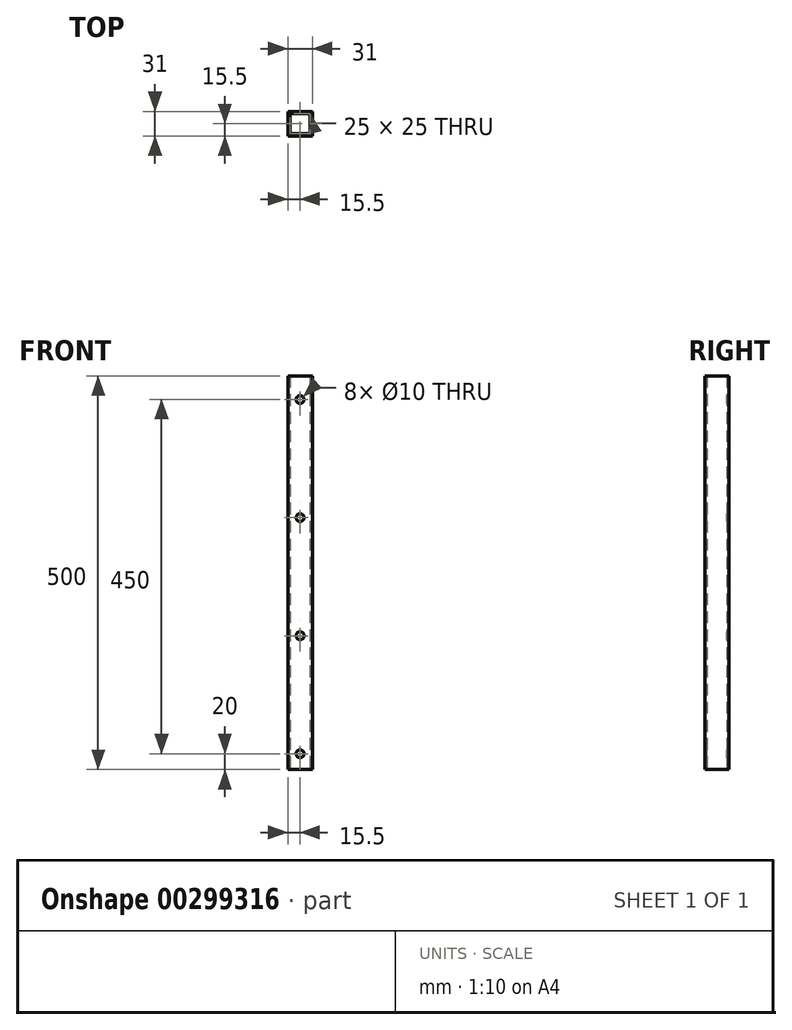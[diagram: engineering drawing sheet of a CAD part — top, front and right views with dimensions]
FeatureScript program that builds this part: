
annotation { "Feature Type Name" : "Feature", "Feature Type Description" : "" }
export const myFeature = defineFeature(function(context is Context, id is Id, definition is map)
    precondition{}
    {
        {
            var Q0;
            Q0=qCreatedBy(makeId("Top.planeOp"),FACE);
            var sketch = newSketch(context, id + "F0", { "sketchPlane" : qUnion([Q0])});
            skLineSegment(sketch, "E0.bottom", {"start": v(12.5, -12.5) * mm, "end": v(-12.5, -12.5) * mm});
            skLineSegment(sketch, "E0.top", {"start": v(12.5, 12.5) * mm, "end": v(-12.5, 12.5) * mm});
            skLineSegment(sketch, "E0.left", {"start": v(12.5, -12.5) * mm, "end": v(12.5, 12.5) * mm});
            skLineSegment(sketch, "E0.right", {"start": v(-12.5, -12.5) * mm, "end": v(-12.5, 12.5) * mm});
            skPoint(sketch, "E0.middle", {"position": v(0, 0) * mm});
            skLineSegment(sketch, "E1.0", {"start": v(15.5, 15.5) * mm, "end": v(-15.5, 15.5) * mm});
            skLineSegment(sketch, "E1.1", {"start": v(15.5, -15.5) * mm, "end": v(15.5, 15.5) * mm});
            skLineSegment(sketch, "E1.2", {"start": v(15.5, -15.5) * mm, "end": v(-15.5, -15.5) * mm});
            skLineSegment(sketch, "E1.3", {"start": v(-15.5, -15.5) * mm, "end": v(-15.5, 15.5) * mm});
            skSolve(sketch);
        }
        {
            var Q0;
            Q0 = qSketchRegion(id + "F0", true);
            extrude(context, id + "F1", {"entities" : qUnion([Q0]), "depth" : 500 * mm});
        }
        {
            var Q0;
            Q0=qCreatedBy(makeId("Front.planeOp"),FACE);
            var sketch = newSketch(context, id + "F2", { "sketchPlane" : qUnion([Q0])});
            skCircle(sketch, "E2", {"center": v(0, 470) * mm, "radius": 5 * mm});
            skCircle(sketch, "E3.0.1.0", {"center": v(0, 320) * mm, "radius": 5 * mm});
            skCircle(sketch, "E3.0.2.0", {"center": v(0, 170) * mm, "radius": 5 * mm});
            skCircle(sketch, "E3.0.3.0", {"center": v(0, 20) * mm, "radius": 5 * mm});
            skLineSegment(sketch, "E3.direction1", {"start": v(0, 470) * mm, "end": v(25, 470) * mm, "construction": true});
            skLineSegment(sketch, "E3.direction2", {"start": v(0, 470) * mm, "end": v(0, 320) * mm, "construction": true});
            skSolve(sketch);
        }
        {
            var Q0;
            Q0 = qSketchRegion(id + "F2", true);
            extrude(context, id + "F3", {"entities" : qUnion([Q0]), "operationType" : NewBodyOperationType.REMOVE, "endBound" : BoundingType.THROUGH_ALL, "depth" : 25 * mm, "hasSecondDirection" : true, "secondDirectionBound" : SecondDirectionBoundingType.THROUGH_ALL, "secondDirectionOppositeDirection" : true, "secondDirectionDepth" : 25 * mm});
        }
    });
